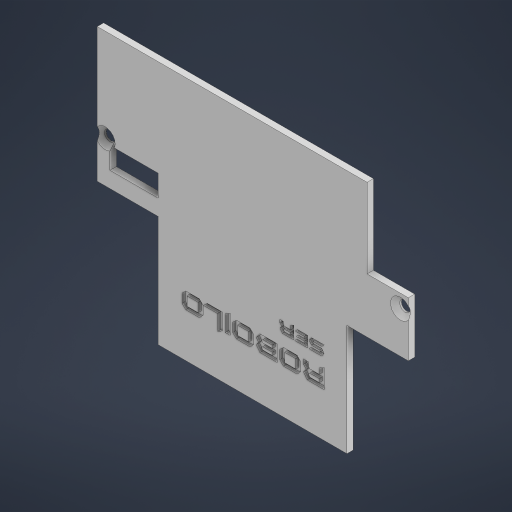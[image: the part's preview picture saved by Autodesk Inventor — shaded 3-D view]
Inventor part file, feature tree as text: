
AUTODESK INVENTOR PART (.ipt)
format: ipt  version: 2023 (Build 270158000, 158)  size: 324,608 bytes
history: native  units: mm
features: other x10, reference x9, sketch x3, extrude x2, hole x1
ambient origin geometry x8: Origin, YZ Plane, XZ Plane, XY Plane, X Axis, Y Axis, Z Axis, Center Point
bodies: Solid1 (feature_tree)
feature tree (25):
  extrude  "Extrusion1"  Depth=0.2mm
  extrude  "Extrusion2"  Depth=13.0mm
  hole  "Hole1"  [1 undecoded]
  sketch  "Sketch1"  dims[d0=0.2mm d1=0.2mm]
  reference  "Reference1"
  reference  "Reference2"
  reference  "Reference3"
  reference  "Reference4"
  reference  "Reference5"
  reference  "Reference6"
  reference  "Reference7"
  sketch  "Sketch2"  dims[d2=2.0mm d3=0.0mm d4=13.0mm]
  sketch  "Sketch3"  dims[d5=2.0mm d6=7.670494mm d7=45.160859mm d8=4.5mm d9=14.0mm d10=1.0mm d11=0.0mm d12=3.4mm d13=6.0mm d14=6.3mm d15=2.0mm d16=90.0deg d17=8.0mm d18=20.594885mm d19=25.0mm d20=13.0mm d23=4.0mm d24=5.0mm d25=11.8mm]
  reference  "Reference8"
  reference  "Reference9"
  parser-record x1  (decoder bookkeeping rows leaked as tree rows — omitted from the tree; the rows remain in map.json)
  other  "Zlozenie.iam"
  other  "PrzekladniaPrawa:1"
  other  "OslonaPrawejPrzekladni:1"
  other  "Kolo:1"
  other  "Opona:1"
  other  "Lewybok:1"
  other  "Prawybok:1"
  other  "Przod:1"
  other  "Tyl:1"
note: 1 required parameter value undecoded (feature->parameter linkage not recoverable at this tier; creation-order binding heuristic only, values carry confidence <= 0.55)
note: 1 file-system path scrubbed to <path> (originals preserved in map.json)
